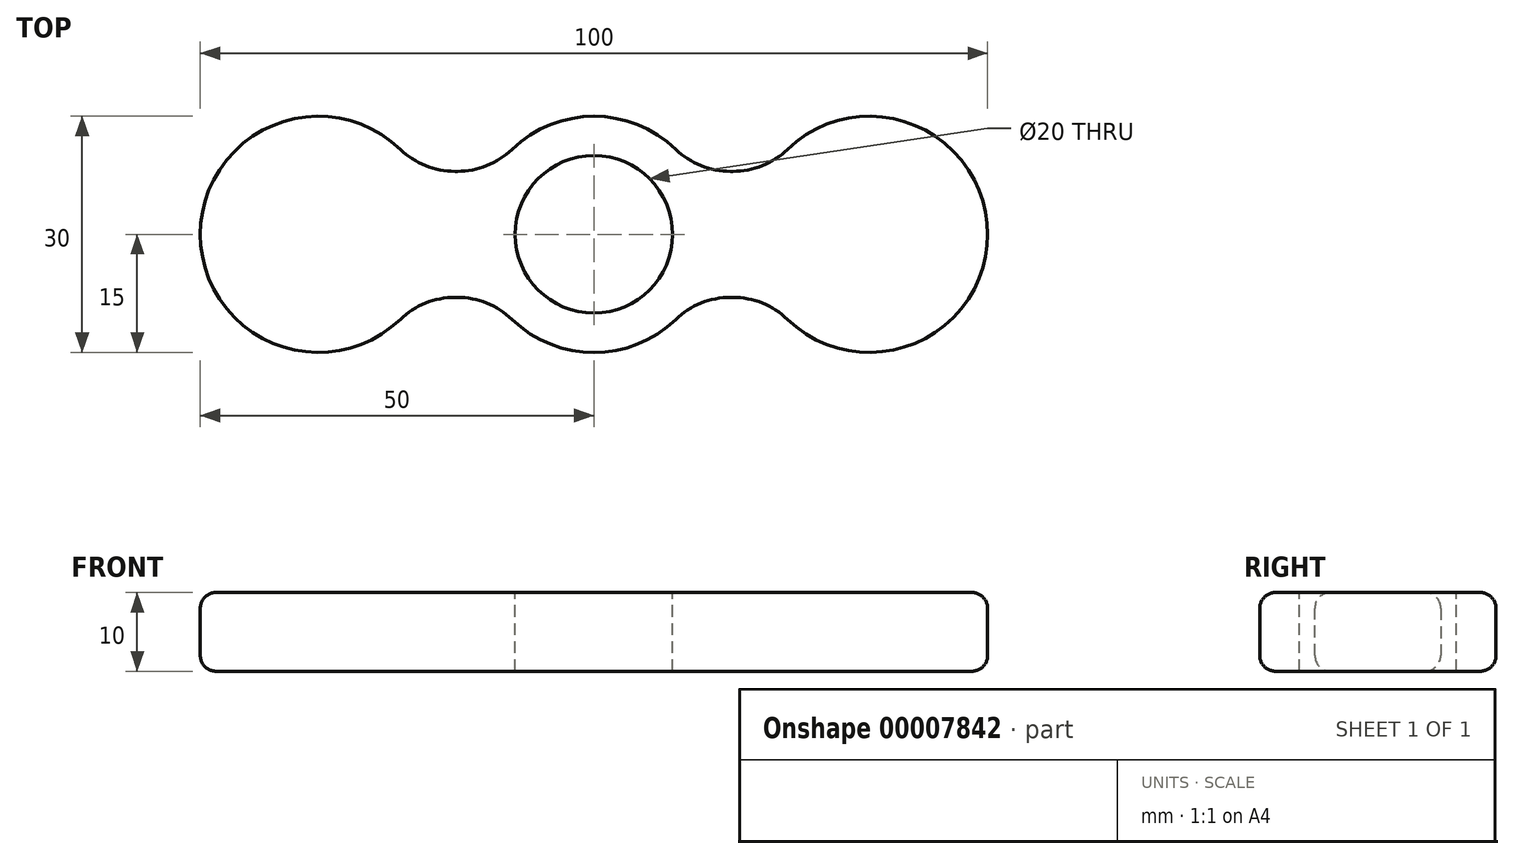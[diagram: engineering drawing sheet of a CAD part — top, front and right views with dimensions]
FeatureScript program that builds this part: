
annotation { "Feature Type Name" : "Feature", "Feature Type Description" : "" }
export const myFeature = defineFeature(function(context is Context, id is Id, definition is map)
    precondition{}
    {
        {
            var Q0;
            Q0=qCreatedBy(makeId("Top.planeOp"),FACE);
            var sketch = newSketch(context, id + "F0", { "sketchPlane" : qUnion([Q0])});
            skCircle(sketch, "E0", {"center": v(0, 0) * mm, "radius": 15 * mm});
            skCircle(sketch, "E1", {"center": v(-35, 0) * mm, "radius": 15 * mm});
            skCircle(sketch, "E2", {"center": v(35, 0) * mm, "radius": 15 * mm});
            skLineSegment(sketch, "E3", {"start": v(-22.31, 8) * mm, "end": v(-12.69, 8) * mm});
            skLineSegment(sketch, "E4", {"start": v(-22.31, -8) * mm, "end": v(-12.69, -8) * mm});
            skLineSegment(sketch, "E5", {"start": v(12.69, 8) * mm, "end": v(22.31, 8) * mm});
            skLineSegment(sketch, "E6", {"start": v(12.69, -8) * mm, "end": v(22.31, -8) * mm});
            skSolve(sketch);
        }
        {
            var Q0;
            {var subQ0=sQuery(id+"F0.wireOp",EDGE,"E1");var subQ1=makeQuery(id+"F0.imprint","INTERSECT",VERTEX,{"derivedFrom":[subQ0,sQuery(id+"F0.wireOp",EDGE,"E3")]});Q0=makeQuery(id+"F0.imprint","IMPRINT",FACE,{"disambiguationData":[TD([[makeQuery(id+"F0.imprint","IMPRINT",EDGE,{"disambiguationData":[TD([[subQ1,-1.0]])],"derivedFrom":subQ0}),1.0]])]});}
            var Q1;
            {var subQ0=sQuery(id+"F0.wireOp",EDGE,"E3");Q1=makeQuery(id+"F0.imprint","IMPRINT",FACE,{"disambiguationData":[TD([[makeQuery(id+"F0.imprint","IMPRINT",EDGE,{"derivedFrom":subQ0}),-1.0]])]});}
            var Q2;
            {var subQ0=sQuery(id+"F0.wireOp",EDGE,"E0");var subQ1=makeQuery(id+"F0.imprint","INTERSECT",VERTEX,{"derivedFrom":[subQ0,sQuery(id+"F0.wireOp",EDGE,"E3")]});Q2=makeQuery(id+"F0.imprint","IMPRINT",FACE,{"disambiguationData":[TD([[makeQuery(id+"F0.imprint","IMPRINT",EDGE,{"disambiguationData":[TD([[subQ1,1.0]])],"derivedFrom":subQ0}),1.0]])]});}
            var Q3;
            {var subQ0=sQuery(id+"F0.wireOp",EDGE,"E5");Q3=makeQuery(id+"F0.imprint","IMPRINT",FACE,{"disambiguationData":[TD([[makeQuery(id+"F0.imprint","IMPRINT",EDGE,{"derivedFrom":subQ0}),-1.0]])]});}
            var Q4;
            {var subQ0=sQuery(id+"F0.wireOp",EDGE,"E2");var subQ1=makeQuery(id+"F0.imprint","INTERSECT",VERTEX,{"derivedFrom":[subQ0,sQuery(id+"F0.wireOp",EDGE,"E5")]});Q4=makeQuery(id+"F0.imprint","IMPRINT",FACE,{"disambiguationData":[TD([[makeQuery(id+"F0.imprint","IMPRINT",EDGE,{"disambiguationData":[TD([[subQ1,-1.0]])],"derivedFrom":subQ0}),1.0]])]});}
            extrude(context, id + "F1", {"entities" : qUnion([Q0, Q1, Q2, Q3, Q4]), "depth" : 10 * mm});
        }
        {
            var Q0;
            Q0=makeQuery(id+"F1.opExtrude","SWEPT_EDGE",EDGE,{"disambiguationData":[OSD([sQuery(id+"F0.wireOp",EDGE,"E2"),sQuery(id+"F0.wireOp",EDGE,"E6")])]});
            var Q1;
            Q1=makeQuery(id+"F1.opExtrude","SWEPT_EDGE",EDGE,{"disambiguationData":[OSD([sQuery(id+"F0.wireOp",EDGE,"E0"),sQuery(id+"F0.wireOp",EDGE,"E4")])]});
            var Q2;
            Q2=makeQuery(id+"F1.opExtrude","SWEPT_EDGE",EDGE,{"disambiguationData":[OSD([sQuery(id+"F0.wireOp",EDGE,"E0"),sQuery(id+"F0.wireOp",EDGE,"E6")])]});
            var Q3;
            Q3=makeQuery(id+"F1.opExtrude","SWEPT_EDGE",EDGE,{"disambiguationData":[OSD([sQuery(id+"F0.wireOp",EDGE,"E1"),sQuery(id+"F0.wireOp",EDGE,"E4")])]});
            var Q4;
            Q4=makeQuery(id+"F1.opExtrude","SWEPT_EDGE",EDGE,{"disambiguationData":[OSD([sQuery(id+"F0.wireOp",EDGE,"E1"),sQuery(id+"F0.wireOp",EDGE,"E3")])]});
            var Q5;
            Q5=makeQuery(id+"F1.opExtrude","SWEPT_EDGE",EDGE,{"disambiguationData":[OSD([sQuery(id+"F0.wireOp",EDGE,"E0"),sQuery(id+"F0.wireOp",EDGE,"E3")])]});
            var Q6;
            Q6=makeQuery(id+"F1.opExtrude","SWEPT_EDGE",EDGE,{"disambiguationData":[OSD([sQuery(id+"F0.wireOp",EDGE,"E0"),sQuery(id+"F0.wireOp",EDGE,"E5")])]});
            var Q7;
            Q7=makeQuery(id+"F1.opExtrude","SWEPT_EDGE",EDGE,{"disambiguationData":[OSD([sQuery(id+"F0.wireOp",EDGE,"E2"),sQuery(id+"F0.wireOp",EDGE,"E5")])]});
            fillet(context, id + "F2", {"entities" : qUnion([Q0, Q1, Q2, Q3, Q4, Q5, Q6, Q7]), "radius" : 10 * mm, "tangentPropagation" : true, "allowEdgeOverflow" : false});
        }
        {
            var Q0;
            Q0=makeQuery(id+"F1.opExtrude","CAP_EDGE",EDGE,{"disambiguationData":[OSD([sQuery(id+"F0.wireOp",EDGE,"E2")])],"isStart":true});
            var Q1;
            Q1=makeQuery(id+"F1.opExtrude","CAP_EDGE",EDGE,{"disambiguationData":[OSD([sQuery(id+"F0.wireOp",EDGE,"E2")])],"isStart":false});
            fillet(context, id + "F3", {"entities" : qUnion([Q0, Q1]), "radius" : 2 * mm, "tangentPropagation" : true, "allowEdgeOverflow" : false});
        }
        {
            var Q0;
            Q0=makeQuery(id+"F1.opExtrude","CAP_FACE",FACE,{"disambiguationData":[OSD([sQuery(id+"F0.wireOp",EDGE,"E0"),sQuery(id+"F0.wireOp",EDGE,"E1"),sQuery(id+"F0.wireOp",EDGE,"E2"),sQuery(id+"F0.wireOp",EDGE,"E3"),sQuery(id+"F0.wireOp",EDGE,"E4"),sQuery(id+"F0.wireOp",EDGE,"E5"),sQuery(id+"F0.wireOp",EDGE,"E6")])],"isStart":false});
            var sketch = newSketch(context, id + "F4", { "sketchPlane" : qUnion([Q0])});
            skCircle(sketch, "E7", {"center": v(0, 0) * mm, "radius": 10 * mm});
            skSolve(sketch);
        }
        {
            var Q0;
            Q0=makeQuery(id+"F4.imprint","IMPRINT",FACE,{"disambiguationData":[TD([[makeQuery(id+"F4.imprint","IMPRINT",EDGE,{"derivedFrom":sQuery(id+"F4.wireOp",EDGE,"E7")}),1.0]])]});
            extrude(context, id + "F5", {"entities" : qUnion([Q0]), "operationType" : NewBodyOperationType.REMOVE, "endBound" : BoundingType.UP_TO_NEXT, "oppositeDirection" : true, "depth" : 25 * mm});
        }
    });
